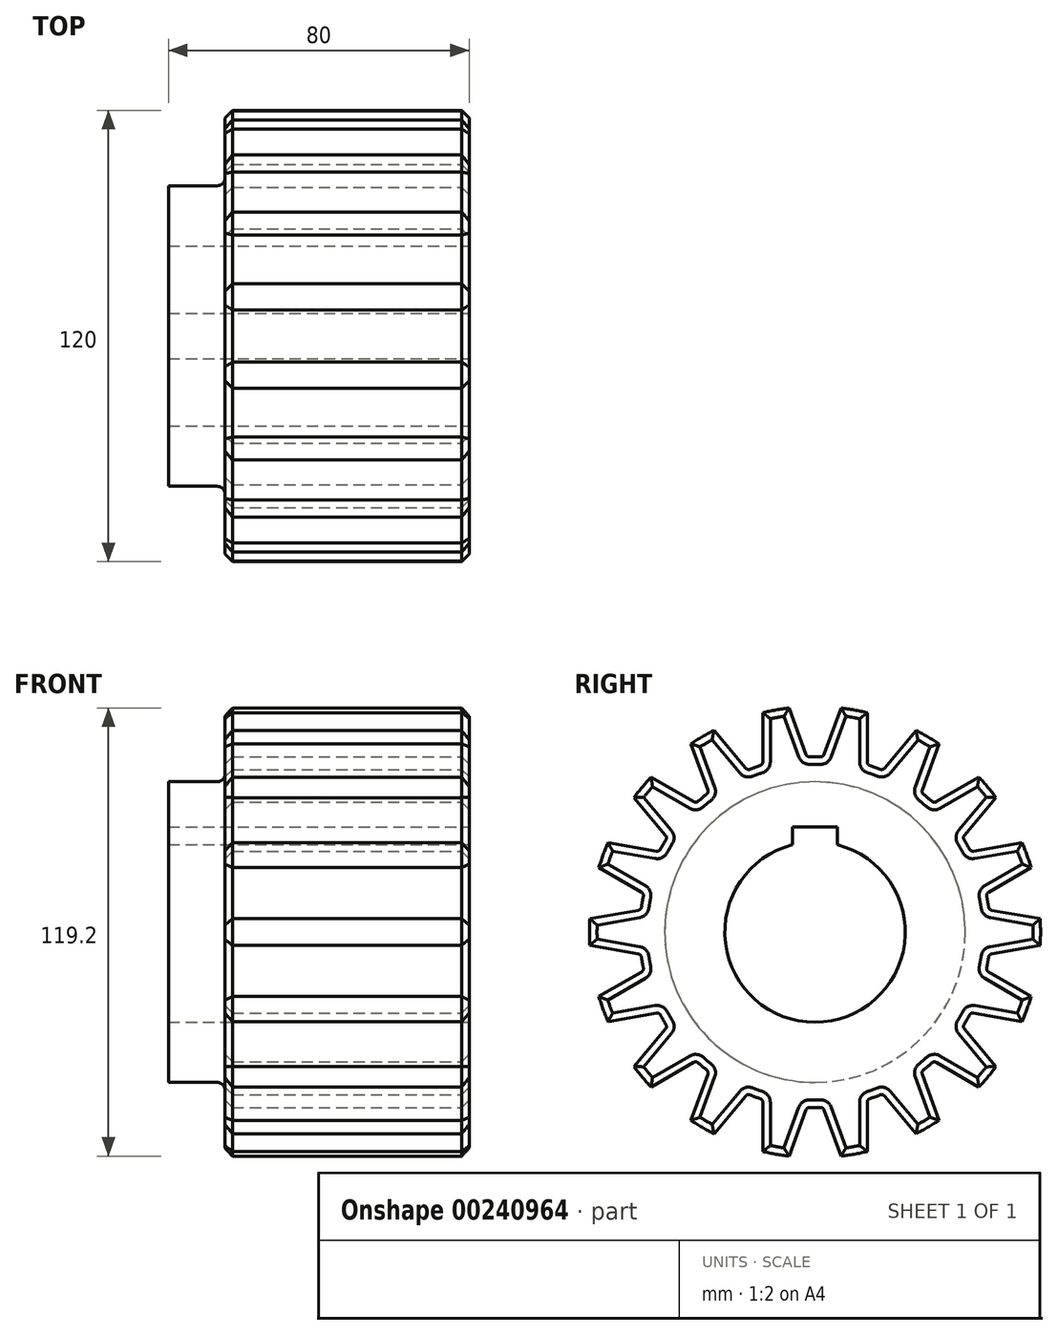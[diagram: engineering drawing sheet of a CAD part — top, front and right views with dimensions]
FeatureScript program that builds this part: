
annotation { "Feature Type Name" : "Feature", "Feature Type Description" : "" }
export const myFeature = defineFeature(function(context is Context, id is Id, definition is map)
    precondition{}
    {
        {
            var Q0;
            Q0=qCreatedBy(makeId("Front.planeOp"),FACE);
            var sketch = newSketch(context, id + "F0", { "sketchPlane" : qUnion([Q0])});
            skLineSegment(sketch, "E0", {"start": v(-80, 0) * mm, "end": v(0, 0) * mm});
            skLineSegment(sketch, "E1", {"start": v(0, 0) * mm, "end": v(0, 60) * mm});
            skLineSegment(sketch, "E2", {"start": v(0, 60) * mm, "end": v(-65, 60) * mm});
            skLineSegment(sketch, "E3", {"start": v(-65, 60) * mm, "end": v(-65, 40) * mm});
            skLineSegment(sketch, "E4", {"start": v(-65, 40) * mm, "end": v(-80, 40) * mm});
            skLineSegment(sketch, "E5", {"start": v(-80, 40) * mm, "end": v(-80, 0) * mm});
            skLineSegment(sketch, "E6", {"start": v(13.12, 0) * mm, "end": v(-97.5, 0) * mm, "construction": true});
            skSolve(sketch);
        }
        {
            var Q0;
            Q0=makeQuery(id+"F0.imprint","IMPRINT",FACE,{"disambiguationData":[TD([[makeQuery(id+"F0.imprint","IMPRINT",EDGE,{"derivedFrom":sQuery(id+"F0.wireOp",EDGE,"E0")}),1.0]])]});
            var Q1;
            Q1=sQuery(id+"F0.wireOp",EDGE,"E6");
            revolve(context, id + "F1", {"entities" : qUnion([Q0]), "axis" : qUnion([Q1]), "revolveType" : RevolveType.FULL});
        }
        {
            var Q0;
            Q0=makeQuery(id+"F1.opRevolve","SWEPT_FACE",FACE,{"disambiguationData":[OSD([sQuery(id+"F0.wireOp",EDGE,"E1")])]});
            var sketch = newSketch(context, id + "F2", { "sketchPlane" : qUnion([Q0])});
            skLineSegment(sketch, "E7.bottom", {"start": v(6, 28) * mm, "end": v(-6, 28) * mm});
            skLineSegment(sketch, "E7.top", {"start": v(6, 20) * mm, "end": v(-6, 20) * mm});
            skLineSegment(sketch, "E7.left", {"start": v(6, 28) * mm, "end": v(6, 20) * mm});
            skLineSegment(sketch, "E7.right", {"start": v(-6, 28) * mm, "end": v(-6, 20) * mm});
            skPoint(sketch, "E7.middle", {"position": v(0, 24) * mm});
            skSolve(sketch);
        }
        {
            var Q0;
            Q0=makeQuery(id+"F1.opRevolve","SWEPT_FACE",FACE,{"disambiguationData":[OSD([sQuery(id+"F0.wireOp",EDGE,"E1")])]});
            var sketch = newSketch(context, id + "F3", { "sketchPlane" : qUnion([Q0])});
            skArc(sketch, "E8", {"start": v(2.18, 46.6) * mm, "mid": v(0, 46.66) * mm, "end": v(-2.18, 46.6) * mm});
            skLineSegment(sketch, "E9", {"start": v(2.18, 46.6) * mm, "end": v(8.32, 63.46) * mm});
            skCircle(sketch, "E10", {"center": v(0, 0) * mm, "radius": 54 * mm, "construction": true});
            skLineSegment(sketch, "E11.MirrorCS", {"start": v(-2.18, 46.6) * mm, "end": v(-8.32, 63.46) * mm});
            skPoint(sketch, "E12", {"position": v(4.8, 53.79) * mm});
            skPoint(sketch, "E13", {"position": v(-4.8, 53.79) * mm});
            skArc(sketch, "E14", {"start": v(8.32, 63.46) * mm, "mid": v(0, 64) * mm, "end": v(-8.32, 63.46) * mm});
            skSolve(sketch);
        }
        {
            var Q0;
            Q0 = qSketchRegion(id + "F3", true);
            extrude(context, id + "F4", {"entities" : qUnion([Q0]), "operationType" : NewBodyOperationType.REMOVE, "endBound" : BoundingType.THROUGH_ALL, "oppositeDirection" : true, "depth" : 25 * mm});
        }
        {
            var Q0;
            Q0=makeQuery(id+"F4.boolean.opBoolean","COPY",EDGE,{"derivedFrom":makeQuery(id+"F4.opExtrude","SWEPT_EDGE",EDGE,{"disambiguationData":[OSD([sQuery(id+"F3.wireOp",EDGE,"E8"),sQuery(id+"F3.wireOp",EDGE,"E9")])]})});
            var Q1;
            Q1=makeQuery(id+"F4.boolean.opBoolean","COPY",EDGE,{"derivedFrom":makeQuery(id+"F4.opExtrude","SWEPT_EDGE",EDGE,{"disambiguationData":[OSD([sQuery(id+"F3.wireOp",EDGE,"E8"),sQuery(id+"F3.wireOp",EDGE,"E11.MirrorCS")])]})});
            fillet(context, id + "F5", {"entities" : qUnion([Q0, Q1]), "radius" : 1 * mm, "tangentPropagation" : true, "allowEdgeOverflow" : false});
        }
        {
            var Q0;
            Q0=makeQuery(id+"F4.boolean.opBoolean","COPY",FACE,{"derivedFrom":makeQuery(id+"F4.opExtrude","SWEPT_FACE",FACE,{"disambiguationData":[OSD([sQuery(id+"F3.wireOp",EDGE,"E9")])]})});
            var Q1;
            Q1=makeQuery(id+"F5.opFillet","BLEND_FACE",FACE,{"disambiguationData":[OSD([sQuery(id+"F3.wireOp",EDGE,"E8"),sQuery(id+"F3.wireOp",EDGE,"E9")])]});
            var Q2;
            Q2=makeQuery(id+"F4.boolean.opBoolean","COPY",FACE,{"derivedFrom":makeQuery(id+"F4.opExtrude","SWEPT_FACE",FACE,{"disambiguationData":[OSD([sQuery(id+"F3.wireOp",EDGE,"E8")])]})});
            var Q3;
            Q3=makeQuery(id+"F5.opFillet","BLEND_FACE",FACE,{"disambiguationData":[OSD([sQuery(id+"F3.wireOp",EDGE,"E8"),sQuery(id+"F3.wireOp",EDGE,"E11.MirrorCS")])]});
            var Q4;
            Q4=makeQuery(id+"F4.boolean.opBoolean","COPY",FACE,{"derivedFrom":makeQuery(id+"F4.opExtrude","SWEPT_FACE",FACE,{"disambiguationData":[OSD([sQuery(id+"F3.wireOp",EDGE,"E11.MirrorCS")])]})});
            var Q5;
            Q5=sQuery(id+"F0.wireOp",EDGE,"E6");
            circularPattern(context, id + "F6", {"patternType" : PatternType.FACE, "faces" : qUnion([Q0, Q1, Q2, Q3, Q4]), "axis" : qUnion([Q5]), "angle" : 360 * degree, "instanceCount" : 18, "equalSpace" : true});
        }
        {
            var Q0;
            Q0=makeQuery(id+"F1.opRevolve","SWEPT_EDGE",EDGE,{"disambiguationData":[OSD([sQuery(id+"F0.wireOp",EDGE,"E3"),sQuery(id+"F0.wireOp",EDGE,"E4")])]});
            fillet(context, id + "F7", {"entities" : qUnion([Q0]), "radius" : 2 * mm, "tangentPropagation" : true, "allowEdgeOverflow" : false});
        }
        {
            var Q0;
            Q0=makeQuery(id+"F1.opRevolve","SWEPT_FACE",FACE,{"disambiguationData":[OSD([sQuery(id+"F0.wireOp",EDGE,"E3")])]});
            var Q1;
            Q1=makeQuery(id+"F1.opRevolve","SWEPT_FACE",FACE,{"disambiguationData":[OSD([sQuery(id+"F0.wireOp",EDGE,"E1")])]});
            chamfer(context, id + "F8", {"entities" : qUnion([Q0, Q1]), "width" : 2 * mm, "tangentPropagation" : true});
        }
        {
            var Q0;
            Q0=makeQuery(id+"F1.opRevolve","SWEPT_FACE",FACE,{"disambiguationData":[OSD([sQuery(id+"F0.wireOp",EDGE,"E1")])]});
            var sketch = newSketch(context, id + "F9", { "sketchPlane" : qUnion([Q0])});
            skCircle(sketch, "E15", {"center": v(0, 0) * mm, "radius": 24 * mm});
            skSolve(sketch);
        }
        {
            var Q0;
            Q0 = qSketchRegion(id + "F9", true);
            extrude(context, id + "F10", {"entities" : qUnion([Q0]), "operationType" : NewBodyOperationType.REMOVE, "endBound" : BoundingType.THROUGH_ALL, "oppositeDirection" : true, "depth" : 25 * mm});
        }
        {
            var Q0;
            Q0 = qSketchRegion(id + "F2", true);
            extrude(context, id + "F11", {"entities" : qUnion([Q0]), "operationType" : NewBodyOperationType.REMOVE, "endBound" : BoundingType.THROUGH_ALL, "oppositeDirection" : true, "depth" : 25 * mm});
        }
    });
